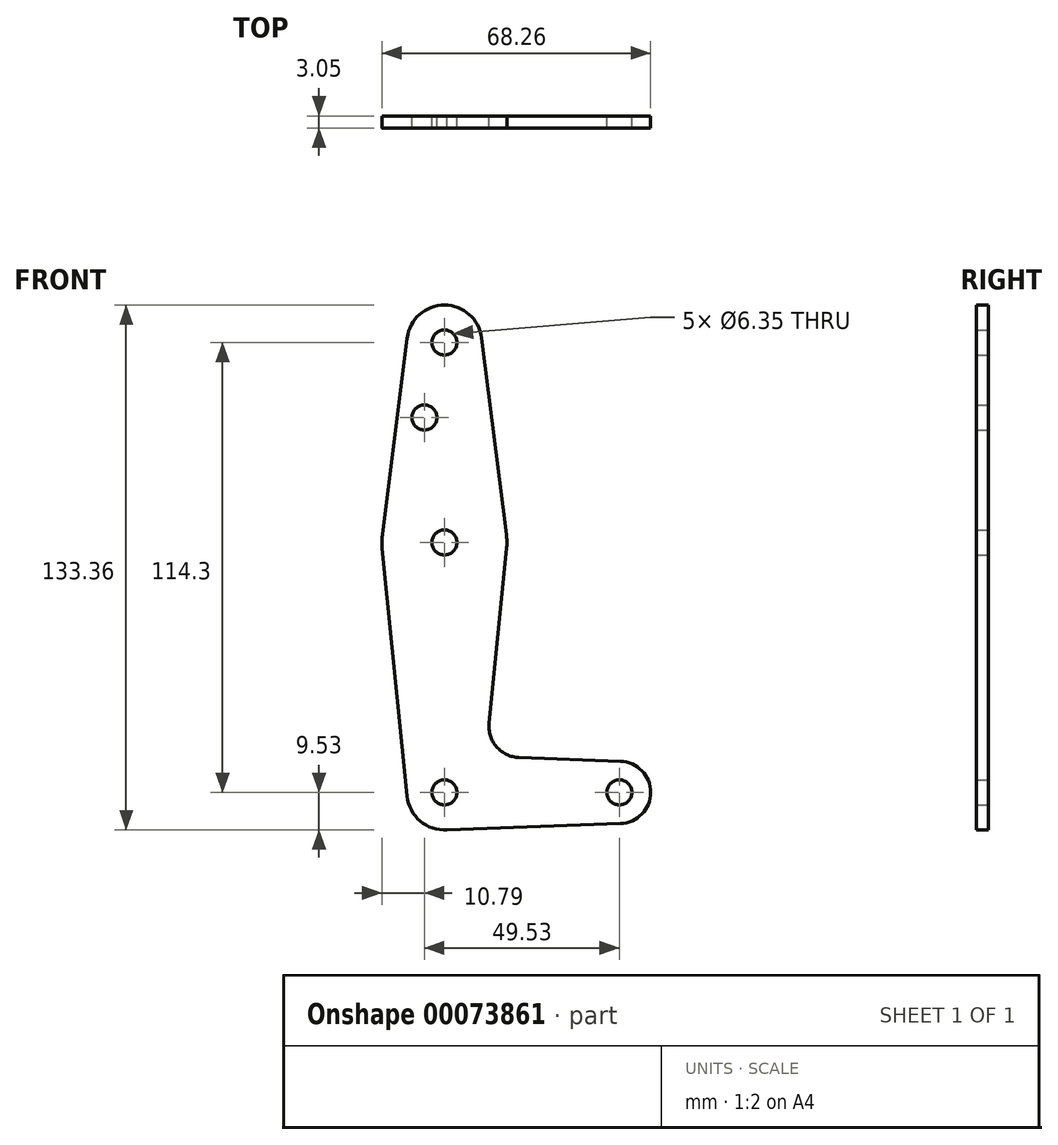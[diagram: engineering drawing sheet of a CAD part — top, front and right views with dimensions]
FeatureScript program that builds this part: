
annotation { "Feature Type Name" : "Feature", "Feature Type Description" : "" }
export const myFeature = defineFeature(function(context is Context, id is Id, definition is map)
    precondition{}
    {
        {
            var Q0;
            Q0=qCreatedBy(makeId("Front.planeOp"),FACE);
            var sketch = newSketch(context, id + "F0", { "sketchPlane" : qUnion([Q0])});
            skLineSegment(sketch, "E0", {"start": v(0, 0) * mm, "end": v(0, 114.3) * mm, "construction": true});
            skLineSegment(sketch, "E1", {"start": v(0, 0) * mm, "end": v(44.45, 0) * mm, "construction": true});
            skCircle(sketch, "E2", {"center": v(0, 114.3) * mm, "radius": 9.53 * mm});
            skCircle(sketch, "E3", {"center": v(0, 63.5) * mm, "radius": 15.88 * mm});
            skCircle(sketch, "E4", {"center": v(0, 0) * mm, "radius": 9.53 * mm});
            skCircle(sketch, "E5", {"center": v(44.45, 0) * mm, "radius": 7.94 * mm});
            skLineSegment(sketch, "E6", {"start": v(-9.48, -0.95) * mm, "end": v(-15.8, 61.91) * mm});
            skLineSegment(sketch, "E7", {"start": v(11.34, 17.6) * mm, "end": v(15.8, 61.91) * mm});
            skLineSegment(sketch, "E8", {"start": v(15.75, 65.48) * mm, "end": v(9.45, 115.5) * mm});
            skLineSegment(sketch, "E9", {"start": v(0, -9.52) * mm, "end": v(44.73, -7.93) * mm});
            skLineSegment(sketch, "E10", {"start": v(44.73, 7.93) * mm, "end": v(18.97, 8.85) * mm});
            skLineSegment(sketch, "E11", {"start": v(-15.75, 65.48) * mm, "end": v(-9.45, 115.5) * mm});
            skArc(sketch, "E12.filletArc", {"start": v(11.34, 17.6) * mm, "mid": v(13.26, 11.57) * mm, "end": v(18.97, 8.85) * mm});
            skCircle(sketch, "E13", {"center": v(0, 114.3) * mm, "radius": 3.18 * mm});
            skCircle(sketch, "E14", {"center": v(0, 63.5) * mm, "radius": 3.18 * mm});
            skCircle(sketch, "E15", {"center": v(0, 0) * mm, "radius": 3.18 * mm});
            skCircle(sketch, "E16", {"center": v(44.45, 0) * mm, "radius": 3.18 * mm});
            skCircle(sketch, "E17", {"center": v(-5.08, 95.25) * mm, "radius": 3.18 * mm});
            skSolve(sketch);
        }
        {
            var Q0;
            Q0 = qSketchRegion(id + "F0", true);
            extrude(context, id + "F1", {"entities" : qUnion([Q0]), "depth" : 3.05 * mm});
        }
    });
